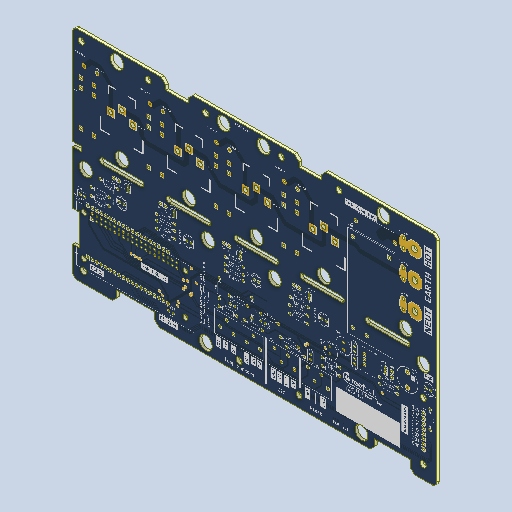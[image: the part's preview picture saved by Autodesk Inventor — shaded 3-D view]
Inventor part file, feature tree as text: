
AUTODESK INVENTOR PART (.ipt)
format: ipt  version: 2023.3 (Build 273359000, 359)  size: 3,891,712 bytes
history: native  units: in
note: dims shown in document units (in); Inventor stores cm internally (conversion verified against a paired STEP export)
features: sketch x301, hole x296, other x8, extrude x6
ambient origin geometry x8: Origin, YZ Plane, XZ Plane, XY Plane, X Axis, Y Axis, Z Axis, Center Point
bodies: Solid1 (feature_tree)
feature tree (611):
  other  "reefvolt_power_essentials_ESP32_BOARD"
  other  "BoardFrontPlane"
  extrude  "BoardOutline"  Depth=0.25in TaperAngle=0.0deg
  hole  "LED100-A"  [1 undecoded]
  hole  "LED100-K"  [1 undecoded]
  hole  "R409-2"  [1 undecoded]
  hole  "R409-1"  [1 undecoded]
  hole  "R408-2"  [1 undecoded]
  hole  "R408-1"  [1 undecoded]
  hole  "R401-2"  [1 undecoded]
  hole  "R401-1"  [1 undecoded]
  hole  "R400-2"  [1 undecoded]
  hole  "R400-1"  [1 undecoded]
  hole  "R407-1"  [1 undecoded]
  hole  "R407-2"  [1 undecoded]
  hole  "R406-1"  [1 undecoded]
  hole  "R406-2"  [1 undecoded]
  hole  "J403-4"  [1 undecoded]
  hole  "J403-3"  [1 undecoded]
  hole  "J403-2"  [1 undecoded]
  hole  "J403-1"  [1 undecoded]
  hole  "J400-4"  [1 undecoded]
  hole  "J400-3"  [1 undecoded]
  hole  "J400-2"  [1 undecoded]
  hole  "J400-1"  [1 undecoded]
  hole  "C400-1"  [1 undecoded]
  hole  "C400-2"  [1 undecoded]
  hole  "C402-1"  [1 undecoded]
  hole  "C402-2"  [1 undecoded]
  hole  "C401-1"  [1 undecoded]
  hole  "C401-2"  [1 undecoded]
  hole  "C301-1"  [1 undecoded]
  hole  "C301-2"  [1 undecoded]
  hole  "C300-1"  [1 undecoded]
  hole  "C300-2"  [1 undecoded]
  hole  "C103-1"  [1 undecoded]
  hole  "C103-2"  [1 undecoded]
  hole  "C102-1"  [1 undecoded]
  hole  "C102-2"  [1 undecoded]
  hole  "R405-2"  [1 undecoded]
  hole  "R405-1"  [1 undecoded]
  hole  "R404-2"  [1 undecoded]
  hole  "R404-1"  [1 undecoded]
  hole  "R403-1"  [1 undecoded]
  hole  "R403-2"  [1 undecoded]
  hole  "R402-1"  [1 undecoded]
  hole  "R402-2"  [1 undecoded]
  hole  "C101-1"  [1 undecoded]
  hole  "C101-2"  [1 undecoded]
  hole  "C100-2"  [1 undecoded]
  hole  "C100-1"  [1 undecoded]
  hole  "J402-3"  [1 undecoded]
  hole  "J402-2"  [1 undecoded]
  hole  "J402-1"  [1 undecoded]
  hole  "J401-3"  [1 undecoded]
  hole  "J401-2"  [1 undecoded]
  hole  "J401-1"  [1 undecoded]
  hole  "U301-J2-1"  [1 undecoded]
  hole  "U301-J2-2"  [1 undecoded]
  hole  "U301-J2-19"  [1 undecoded]
  hole  "U301-J2-3"  [1 undecoded]
  hole  "U301-J2-4"  [1 undecoded]
  hole  "U301-J2-5"  [1 undecoded]
  hole  "U301-J2-6"  [1 undecoded]
  hole  "U301-J2-7"  [1 undecoded]
  hole  "U301-J2-8"  [1 undecoded]
  hole  "U301-J2-9"  [1 undecoded]
  hole  "U301-J2-10"  [1 undecoded]
  hole  "U301-J2-11"  [1 undecoded]
  hole  "U301-J2-12"  [1 undecoded]
  hole  "U301-J2-13"  [1 undecoded]
  hole  "U301-J2-14"  [1 undecoded]
  hole  "U301-J2-15"  [1 undecoded]
  hole  "U301-J2-16"  [1 undecoded]
  hole  "U301-J2-17"  [1 undecoded]
  hole  "U301-J2-18"  [1 undecoded]
  hole  "U301-J3-1"  [1 undecoded]
  hole  "U301-J3-2"  [1 undecoded]
  hole  "U301-J3-3"  [1 undecoded]
  hole  "U301-J3-4"  [1 undecoded]
  hole  "U301-J3-5"  [1 undecoded]
  hole  "U301-J3-6"  [1 undecoded]
  hole  "U301-J3-7"  [1 undecoded]
  hole  "U301-J3-8"  [1 undecoded]
  hole  "U301-J3-9"  [1 undecoded]
  hole  "U301-J3-10"  [1 undecoded]
  hole  "U301-J3-11"  [1 undecoded]
  hole  "U301-J3-12"  [1 undecoded]
  hole  "U301-J3-13"  [1 undecoded]
  hole  "U301-J3-14"  [1 undecoded]
  hole  "U301-J3-15"  [1 undecoded]
  hole  "U301-J3-16"  [1 undecoded]
  hole  "U301-J3-17"  [1 undecoded]
  hole  "U301-J3-18"  [1 undecoded]
  hole  "U301-J3-19"  [1 undecoded]
  hole  "U300-4"  [1 undecoded]
  hole  "U300-3"  [1 undecoded]
  hole  "U300-2"  [1 undecoded]
  hole  "U300-1"  [1 undecoded]
  hole  "U300-_OMEBCNFT"  [1 undecoded]
  hole  "U300-_WJWYHENG"  [1 undecoded]
  hole  "U300-_VXPHIMLI"  [1 undecoded]
  hole  "U300-_OVXJNJRO"  [1 undecoded]
  hole  "U300-5"  [1 undecoded]
  hole  "U300-6"  [1 undecoded]
  hole  "U300-7"  [1 undecoded]
  hole  "U300-8"  [1 undecoded]
  hole  "U300-9"  [1 undecoded]
  hole  "U300-10"  [1 undecoded]
  hole  "U300-11"  [1 undecoded]
  hole  "U300-12"  [1 undecoded]
  hole  "U300-13"  [1 undecoded]
  hole  "U300-14"  [1 undecoded]
  hole  "U300-15"  [1 undecoded]
  hole  "U300-16"  [1 undecoded]
  hole  "U300-17"  [1 undecoded]
  hole  "U300-18"  [1 undecoded]
  hole  "U300-19"  [1 undecoded]
  hole  "U300-20"  [1 undecoded]
  hole  "U300-21"  [1 undecoded]
  hole  "U300-22"  [1 undecoded]
  hole  "U300-23"  [1 undecoded]
  hole  "U300-24"  [1 undecoded]
  hole  "U300-25"  [1 undecoded]
  hole  "U300-26"  [1 undecoded]
  hole  "U300-27"  [1 undecoded]
  hole  "U300-28"  [1 undecoded]
  hole  "U300-29"  [1 undecoded]
  hole  "U300-30"  [1 undecoded]
  hole  "U300-31"  [1 undecoded]
  hole  "U300-32"  [1 undecoded]
  hole  "U300-33"  [1 undecoded]
  hole  "U300-34"  [1 undecoded]
  hole  "U300-35"  [1 undecoded]
  hole  "U300-36"  [1 undecoded]
  hole  "U300-37"  [1 undecoded]
  hole  "U300-38"  [1 undecoded]
  hole  "U300-39"  [1 undecoded]
  hole  "U300-40"  [1 undecoded]
  hole  "Free-MNT+25_VMCLGUVO"  [1 undecoded]
  hole  "Free-MNT+26"  [1 undecoded]
  hole  "Free-MNT+25_KEWVVEYY"  [1 undecoded]
  hole  "Free-MNT+24"  [1 undecoded]
  hole  "Free-MNT+23"  [1 undecoded]
  hole  "Free-MNT+22"  [1 undecoded]
  hole  "Free-MNT+21"  [1 undecoded]
  hole  "Free-MNT+20"  [1 undecoded]
  hole  "Free-MNT+19"  [1 undecoded]
  hole  "Free-MNT+16"  [1 undecoded]
  hole  "J500-8"  [1 undecoded]
  hole  "J500-7"  [1 undecoded]
  hole  "J500-6"  [1 undecoded]
  hole  "J500-5"  [1 undecoded]
  hole  "J500-4"  [1 undecoded]
  hole  "J500-3"  [1 undecoded]
  hole  "J500-2"  [1 undecoded]
  hole  "J500-1"  [1 undecoded]
  hole  "U100-1"  [1 undecoded]
  hole  "U100-2"  [1 undecoded]
  hole  "U100-3"  [1 undecoded]
  hole  "Free-MNT+14_RVGMHBWC"  [1 undecoded]
  hole  "Free-MNT+14_EXUOOQPC"  [1 undecoded]
  hole  "Free-MNT+14_MIJJWCTW"  [1 undecoded]
  hole  "Free-MNT+14_XWPMBVWG"  [1 undecoded]
  hole  "Free-MNT+14_SCTWPPTG"  [1 undecoded]
  hole  "Free-MNT+14_UGSODQMV"  [1 undecoded]
  hole  "Free-MNT+7"  [1 undecoded]
  hole  "XF100-1"  [1 undecoded]
  hole  "XF100-2"  [1 undecoded]
  hole  "M200_PLD-1"  [1 undecoded]
  hole  "M200_PLD-2"  [1 undecoded]
  hole  "M200_PLC-2"  [1 undecoded]
  hole  "M200_PLC-1"  [1 undecoded]
  hole  "M200_PLB-1"  [1 undecoded]
  hole  "M200_PLB-2"  [1 undecoded]
  hole  "M200_PLA-2"  [1 undecoded]
  hole  "M200_PLA-1"  [1 undecoded]
  hole  "J200_PLD-3"  [1 undecoded]
  hole  "J200_PLD-2"  [1 undecoded]
  hole  "J200_PLD-1"  [1 undecoded]
  hole  "J200_PLC-1"  [1 undecoded]
  hole  "J200_PLC-2"  [1 undecoded]
  hole  "J200_PLC-3"  [1 undecoded]
  hole  "J200_PLB-3"  [1 undecoded]
  hole  "J200_PLB-2"  [1 undecoded]
  hole  "J200_PLB-1"  [1 undecoded]
  hole  "J200_PLA-1"  [1 undecoded]
  hole  "J200_PLA-2"  [1 undecoded]
  hole  "J200_PLA-3"  [1 undecoded]
  hole  "U101-4"  [1 undecoded]
  hole  "U101-3"  [1 undecoded]
  hole  "U101-2"  [1 undecoded]
  hole  "U101-1"  [1 undecoded]
  hole  "J_IN102-1"  [1 undecoded]
  hole  "J_IN102-2"  [1 undecoded]
  hole  "J_IN101-1"  [1 undecoded]
  hole  "J_IN101-2"  [1 undecoded]
  hole  "J_IN100-1"  [1 undecoded]
  hole  "J_IN100-2"  [1 undecoded]
  hole  "RL200_PLA-4"  [1 undecoded]
  hole  "RL200_PLA-5"  [1 undecoded]
  hole  "RL200_PLA-3"  [1 undecoded]
  hole  "RL200_PLA-6"  [1 undecoded]
  hole  "RL200_PLA-8"  [1 undecoded]
  hole  "RL200_PLA-1"  [1 undecoded]
  hole  "RL200_PLD-4"  [1 undecoded]
  hole  "RL200_PLD-5"  [1 undecoded]
  hole  "RL200_PLD-3"  [1 undecoded]
  hole  "RL200_PLD-6"  [1 undecoded]
  hole  "RL200_PLD-8"  [1 undecoded]
  hole  "RL200_PLD-1"  [1 undecoded]
  hole  "RL200_PLC-4"  [1 undecoded]
  hole  "RL200_PLC-5"  [1 undecoded]
  hole  "RL200_PLC-3"  [1 undecoded]
  hole  "RL200_PLC-6"  [1 undecoded]
  hole  "RL200_PLC-8"  [1 undecoded]
  hole  "RL200_PLC-1"  [1 undecoded]
  hole  "RL200_PLB-4"  [1 undecoded]
  hole  "RL200_PLB-5"  [1 undecoded]
  hole  "RL200_PLB-3"  [1 undecoded]
  hole  "RL200_PLB-6"  [1 undecoded]
  hole  "RL200_PLB-8"  [1 undecoded]
  hole  "RL200_PLB-1"  [1 undecoded]
  hole  "Free-MNT+14_KNTGPJBG"  [1 undecoded]
  hole  "Free-MNT+13"  [1 undecoded]
  hole  "Free-MNT+15"  [1 undecoded]
  hole  "Free-MNT+7_OGEKVTGU"  [1 undecoded]
  hole  "Free-MNT+7_ASLNLXPE"  [1 undecoded]
  hole  "SP400--"  [1 undecoded]
  hole  "SP400-+"  [1 undecoded]
  hole  "R411-2"  [1 undecoded]
  hole  "R411-1"  [1 undecoded]
  hole  "R410-2"  [1 undecoded]
  hole  "R410-1"  [1 undecoded]
  hole  "Q400-1"  [1 undecoded]
  hole  "Q400-2"  [1 undecoded]
  hole  "Q400-3"  [1 undecoded]
  hole  "D400-2"  [1 undecoded]
  hole  "D400-1"  [1 undecoded]
  hole  "R100-2"  [1 undecoded]
  hole  "R100-1"  [1 undecoded]
  extrude  "Free-MNT+11_RITJXHYI"  [1 undecoded]
  extrude  "Free-MNT+11_QMOWRTVF"  [1 undecoded]
  extrude  "Free-MNT+10"  [1 undecoded]
  extrude  "Free-MNT+9"  [1 undecoded]
  hole  "Free-MNT+14_SDQKQDHW"  [1 undecoded]
  hole  "Free-MNT+15_ENNIOCQM"  [1 undecoded]
  extrude  "Free-MNT+11_LVIULGXW"  [1 undecoded]
  hole  "Free-MNT+14_GXYHPMGR"  [1 undecoded]
  hole  "Free-MNT+14_QXCUKRLQ"  [1 undecoded]
  hole  "Free-MNT+14_BKPOHODQ"  [1 undecoded]
  hole  "Free-MNT+14_MHRQPGBW"  [1 undecoded]
  other  "Decal_Top"
  other  "Decal_Bottom"
  hole  "R202_PLD-2"  [1 undecoded]
  hole  "R202_PLD-1"  [1 undecoded]
  hole  "R202_PLC-2"  [1 undecoded]
  hole  "R202_PLC-1"  [1 undecoded]
  hole  "R202_PLB-2"  [1 undecoded]
  hole  "R202_PLB-1"  [1 undecoded]
  hole  "R202_PLA-2"  [1 undecoded]
  hole  "R202_PLA-1"  [1 undecoded]
  hole  "R201_PLD-1"  [1 undecoded]
  hole  "R201_PLD-2"  [1 undecoded]
  hole  "R201_PLC-2"  [1 undecoded]
  hole  "R201_PLC-1"  [1 undecoded]
  hole  "R201_PLB-1"  [1 undecoded]
  hole  "R201_PLB-2"  [1 undecoded]
  hole  "R201_PLA-2"  [1 undecoded]
  hole  "R201_PLA-1"  [1 undecoded]
  hole  "Q200_PLD-3"  [1 undecoded]
  hole  "Q200_PLD-2"  [1 undecoded]
  hole  "Q200_PLD-1"  [1 undecoded]
  hole  "Q200_PLC-1"  [1 undecoded]
  hole  "Q200_PLC-2"  [1 undecoded]
  hole  "Q200_PLC-3"  [1 undecoded]
  hole  "Q200_PLB-3"  [1 undecoded]
  hole  "Q200_PLB-2"  [1 undecoded]
  hole  "Q200_PLB-1"  [1 undecoded]
  hole  "Q200_PLA-1"  [1 undecoded]
  hole  "Q200_PLA-2"  [1 undecoded]
  hole  "Q200_PLA-3"  [1 undecoded]
  hole  "D200_PLD-1"  [1 undecoded]
  hole  "D200_PLD-2"  [1 undecoded]
  hole  "D200_PLC-2"  [1 undecoded]
  hole  "D200_PLC-1"  [1 undecoded]
  hole  "D200_PLB-1"  [1 undecoded]
  hole  "D200_PLB-2"  [1 undecoded]
  hole  "D200_PLA-1"  [1 undecoded]
  hole  "D200_PLA-2"  [1 undecoded]
  hole  "R200_PLD-1"  [1 undecoded]
  hole  "R200_PLD-2"  [1 undecoded]
  hole  "R200_PLC-2"  [1 undecoded]
  hole  "R200_PLC-1"  [1 undecoded]
  hole  "R200_PLB-1"  [1 undecoded]
  hole  "R200_PLB-2"  [1 undecoded]
  hole  "R200_PLA-2"  [1 undecoded]
  hole  "R200_PLA-1"  [1 undecoded]
  hole  "LED200_PLD-K"  [1 undecoded]
  hole  "LED200_PLD-A"  [1 undecoded]
  hole  "LED200_PLC-A"  [1 undecoded]
  hole  "LED200_PLC-K"  [1 undecoded]
  hole  "LED200_PLB-K"  [1 undecoded]
  hole  "LED200_PLB-A"  [1 undecoded]
  hole  "LED200_PLA-K"  [1 undecoded]
  hole  "LED200_PLA-A"  [1 undecoded]
  sketch  "Sketch61"  dims[d0=0.0614in d1=0.0in]
  sketch  "Sketch62"  dims[d405=0.032in d406=0.75in d407=0.375in d408=0.25in d409=0.5635in d410=1.0in d411=0.0in]
  sketch  "Sketch71"  dims[d412=0.032in d413=0.75in d414=0.375in d415=0.25in d416=0.5635in d417=1.0in d418=0.0in]
  sketch  "Sketch72"  dims[d475=0.032in d476=0.75in d477=0.375in d478=0.25in d479=0.5635in d480=1.0in d481=0.0in]
  sketch  "Sketch73"  dims[d482=0.032in d483=0.75in d484=0.375in d485=0.25in d486=0.5635in d487=1.0in d488=0.0in]
  sketch  "Sketch74"  dims[d489=0.032in d490=0.75in d491=0.375in d492=0.25in d493=0.5635in d494=1.0in d495=0.0in]
  sketch  "Sketch75"  dims[d496=0.032in d497=0.75in d498=0.375in d499=0.25in d500=0.5635in d501=1.0in d502=0.0in]
  sketch  "Sketch76"  dims[d503=0.032in d504=0.75in d505=0.375in d506=0.25in d507=0.5635in d508=1.0in d509=0.0in]
  sketch  "Sketch77"  dims[d510=0.032in d511=0.75in d512=0.375in d513=0.25in d514=0.5635in d515=1.0in d516=0.0in]
  sketch  "Sketch78"  dims[d517=0.032in d518=0.75in d519=0.375in d520=0.25in d521=0.5635in d522=1.0in d523=0.0in]
  sketch  "Sketch79"  dims[d524=0.032in d525=0.75in d526=0.375in d527=0.25in d528=0.5635in d529=1.0in d530=0.0in]
  sketch  "Sketch80"  dims[d531=0.032in d532=0.75in d533=0.375in d534=0.25in d535=0.5635in d536=1.0in d537=0.0in]
  sketch  "Sketch81"  dims[d538=0.032in d539=0.75in d540=0.375in d541=0.25in d542=0.5635in d543=1.0in d544=0.0in]
  sketch  "Sketch82"  dims[d545=0.032in d546=0.75in d547=0.375in d548=0.25in d549=0.5635in d550=1.0in d551=0.0in]
  sketch  "Sketch83"  dims[d552=0.032in d553=0.75in d554=0.375in d555=0.25in d556=0.5635in d557=1.0in d558=0.0in]
  sketch  "Sketch84"  dims[d559=0.0394in d560=0.75in d561=0.375in d562=0.25in d563=0.5635in d564=1.0in d565=0.0in]
  sketch  "Sketch85"  dims[d566=0.0394in d567=0.75in d568=0.375in d569=0.25in d570=0.5635in d571=1.0in d572=0.0in]
  sketch  "Sketch86"  dims[d573=0.0394in d574=0.75in d575=0.375in d576=0.25in d577=0.5635in d578=1.0in d579=0.0in]
  sketch  "Sketch87"  dims[d580=0.0394in d581=0.75in d582=0.375in d583=0.25in d584=0.5635in d585=1.0in d586=0.0in]
  sketch  "Sketch88"  dims[d587=0.0394in d588=0.75in d589=0.375in d590=0.25in d591=0.5635in d592=1.0in d593=0.0in]
  sketch  "Sketch89"  dims[d594=0.0394in d595=0.75in d596=0.375in d597=0.25in d598=0.5635in d599=1.0in d600=0.0in]
  sketch  "Sketch90"  dims[d601=0.0394in d602=0.75in d603=0.375in d604=0.25in d605=0.5635in d606=1.0in d607=0.0in]
  sketch  "Sketch91"  dims[d608=0.0394in d609=0.75in d610=0.375in d611=0.25in d612=0.5635in d613=1.0in d614=0.0in]
  sketch  "Sketch92"  dims[d615=0.0315in d616=0.75in d617=0.375in d618=0.25in d619=0.5635in d620=1.0in d621=0.0in]
  sketch  "Sketch93"  dims[d622=0.0315in d623=0.75in d624=0.375in d625=0.25in d626=0.5635in d627=1.0in d628=0.0in]
  sketch  "Sketch94"  dims[d629=0.0315in d630=0.75in d631=0.375in d632=0.25in d633=0.5635in d634=1.0in d635=0.0in]
  sketch  "Sketch95"  dims[d636=0.0315in d637=0.75in d638=0.375in d639=0.25in d640=0.5635in d641=1.0in d642=0.0in]
  sketch  "Sketch96"  dims[d643=0.0315in d644=0.75in d645=0.375in d646=0.25in d647=0.5635in d648=1.0in d649=0.0in]
  sketch  "Sketch97"  dims[d650=0.0315in d651=0.75in d652=0.375in d653=0.25in d654=0.5635in d655=1.0in d656=0.0in]
  sketch  "Sketch98"  dims[d657=0.0315in d658=0.75in d659=0.375in d660=0.25in d661=0.5635in d662=1.0in d663=0.0in]
  sketch  "Sketch99"  dims[d664=0.0315in d665=0.75in d666=0.375in d667=0.25in d668=0.5635in d669=1.0in d670=0.0in]
  sketch  "Sketch100"  dims[d671=0.0315in d672=0.75in d673=0.375in d674=0.25in d675=0.5635in d676=1.0in d677=0.0in]
  sketch  "Sketch101"  dims[d678=0.0315in d679=0.75in d680=0.375in d681=0.25in d682=0.5635in d683=1.0in d684=0.0in]
  sketch  "Sketch102"  dims[d685=0.0315in d686=0.75in d687=0.375in d688=0.25in d689=0.5635in d690=1.0in d691=0.0in]
  sketch  "Sketch103"  dims[d692=0.0315in d693=0.75in d694=0.375in d695=0.25in d696=0.5635in d697=1.0in d698=0.0in]
  sketch  "Sketch104"  dims[d699=0.0315in d700=0.75in d701=0.375in d702=0.25in d703=0.5635in d704=1.0in d705=0.0in]
  sketch  "Sketch105"  dims[d706=0.0315in d707=0.75in d708=0.375in d709=0.25in d710=0.5635in d711=1.0in d712=0.0in]
  sketch  "Sketch106"  dims[d713=0.032in d714=0.75in d715=0.375in d716=0.25in d717=0.5635in d718=1.0in d719=0.0in]
  sketch  "Sketch107"  dims[d720=0.032in d721=0.75in d722=0.375in d723=0.25in d724=0.5635in d725=1.0in d726=0.0in]
  sketch  "Sketch108"  dims[d727=0.032in d728=0.75in d729=0.375in d730=0.25in d731=0.5635in d732=1.0in d733=0.0in]
  sketch  "Sketch109"  dims[d734=0.032in d735=0.75in d736=0.375in d737=0.25in d738=0.5635in d739=1.0in d740=0.0in]
  sketch  "Sketch110"  dims[d741=0.032in d742=0.75in d743=0.375in d744=0.25in d745=0.5635in d746=1.0in d747=0.0in]
  sketch  "Sketch111"  dims[d748=0.032in d749=0.75in d750=0.375in d751=0.25in d752=0.5635in d753=1.0in d754=0.0in]
  sketch  "Sketch112"  dims[d755=0.032in d756=0.75in d757=0.375in d758=0.25in d759=0.5635in d760=1.0in d761=0.0in]
  sketch  "Sketch113"  dims[d762=0.032in d763=0.75in d764=0.375in d765=0.25in d766=0.5635in d767=1.0in d768=0.0in]
  sketch  "Sketch114"  dims[d769=0.0315in d770=0.75in d771=0.375in d772=0.25in d773=0.5635in d774=1.0in d775=0.0in]
  sketch  "Sketch115"  dims[d776=0.0315in d777=0.75in d778=0.375in d779=0.25in d780=0.5635in d781=1.0in d782=0.0in]
  sketch  "Sketch116"  dims[d783=0.0315in d784=0.75in d785=0.375in d786=0.25in d787=0.5635in d788=1.0in d789=0.0in]
  sketch  "Sketch117"  dims[d790=0.0315in d791=0.75in d792=0.375in d793=0.25in d794=0.5635in d795=1.0in d796=0.0in]
  sketch  "Sketch118"  dims[d797=0.0394in d798=0.75in d799=0.375in d800=0.25in d801=0.5635in d802=1.0in d803=0.0in]
  sketch  "Sketch119"  dims[d804=0.0394in d805=0.75in d806=0.375in d807=0.25in d808=0.5635in d809=1.0in d810=0.0in]
  sketch  "Sketch120"  dims[d811=0.0394in d812=0.75in d813=0.375in d814=0.25in d815=0.5635in d816=1.0in d817=0.0in]
  sketch  "Sketch121"  dims[d818=0.0394in d819=0.75in d820=0.375in d821=0.25in d822=0.5635in d823=1.0in d824=0.0in]
  sketch  "Sketch122"  dims[d825=0.0394in d826=0.75in d827=0.375in d828=0.25in d829=0.5635in d830=1.0in d831=0.0in]
  sketch  "Sketch123"  dims[d832=0.0394in d833=0.75in d834=0.375in d835=0.25in d836=0.5635in d837=1.0in d838=0.0in]
  sketch  "Sketch124"  dims[d839=0.0409in d840=0.75in d841=0.375in d842=0.25in d843=0.5635in d844=1.0in d845=0.0in]
  sketch  "Sketch125"  dims[d846=0.0409in d847=0.75in d848=0.375in d849=0.25in d850=0.5635in d851=1.0in d852=0.0in]
  sketch  "Sketch126"  dims[d853=0.0409in d854=0.75in d855=0.375in d856=0.25in d857=0.5635in d858=1.0in d859=0.0in]
  sketch  "Sketch127"  dims[d860=0.0409in d861=0.75in d862=0.375in d863=0.25in d864=0.5635in d865=1.0in d866=0.0in]
  sketch  "Sketch128"  dims[d867=0.0409in d868=0.75in d869=0.375in d870=0.25in d871=0.5635in d872=1.0in d873=0.0in]
  sketch  "Sketch129"  dims[d874=0.0409in d875=0.75in d876=0.375in d877=0.25in d878=0.5635in d879=1.0in d880=0.0in]
  sketch  "Sketch130"  dims[d881=0.0409in d882=0.75in d883=0.375in d884=0.25in d885=0.5635in d886=1.0in d887=0.0in]
  sketch  "Sketch131"  dims[d888=0.0409in d889=0.75in d890=0.375in d891=0.25in d892=0.5635in d893=1.0in d894=0.0in]
  sketch  "Sketch132"  dims[d895=0.0409in d896=0.75in d897=0.375in d898=0.25in d899=0.5635in d900=1.0in d901=0.0in]
  sketch  "Sketch133"  dims[d902=0.0409in d903=0.75in d904=0.375in d905=0.25in d906=0.5635in d907=1.0in d908=0.0in]
  sketch  "Sketch134"  dims[d909=0.0409in d910=0.75in d911=0.375in d912=0.25in d913=0.5635in d914=1.0in d915=0.0in]
  sketch  "Sketch135"  dims[d916=0.0409in d917=0.75in d918=0.375in d919=0.25in d920=0.5635in d921=1.0in d922=0.0in]
  sketch  "Sketch136"  dims[d923=0.0409in d924=0.75in d925=0.375in d926=0.25in d927=0.5635in d928=1.0in d929=0.0in]
  sketch  "Sketch137"  dims[d930=0.0409in d931=0.75in d932=0.375in d933=0.25in d934=0.5635in d935=1.0in d936=0.0in]
  sketch  "Sketch138"  dims[d937=0.0409in d938=0.75in d939=0.375in d940=0.25in d941=0.5635in d942=1.0in d943=0.0in]
  sketch  "Sketch139"  dims[d944=0.0409in d945=0.75in d946=0.375in d947=0.25in d948=0.5635in d949=1.0in d950=0.0in]
  sketch  "Sketch140"  dims[d951=0.0409in d952=0.75in d953=0.375in d954=0.25in d955=0.5635in d956=1.0in d957=0.0in]
  sketch  "Sketch141"  dims[d958=0.0409in d959=0.75in d960=0.375in d961=0.25in d962=0.5635in d963=1.0in d964=0.0in]
  sketch  "Sketch142"  dims[d965=0.0409in d966=0.75in d967=0.375in d968=0.25in d969=0.5635in d970=1.0in d971=0.0in]
  sketch  "Sketch143"  dims[d972=0.0409in d973=0.75in d974=0.375in d975=0.25in d976=0.5635in d977=1.0in d978=0.0in]
  sketch  "Sketch144"  dims[d979=0.0409in d980=0.75in d981=0.375in d982=0.25in d983=0.5635in d984=1.0in d985=0.0in]
  sketch  "Sketch145"  dims[d986=0.0409in d987=0.75in d988=0.375in d989=0.25in d990=0.5635in d991=1.0in d992=0.0in]
  sketch  "Sketch146"  dims[d993=0.0409in d994=0.75in d995=0.375in d996=0.25in d997=0.5635in d998=1.0in d999=0.0in]
  sketch  "Sketch147"  dims[d1000=0.0409in d1001=0.75in d1002=0.375in d1003=0.25in d1004=0.5635in d1005=1.0in d1006=0.0in]
  sketch  "Sketch148"  dims[d1007=0.0409in d1008=0.75in d1009=0.375in d1010=0.25in d1011=0.5635in d1012=1.0in d1013=0.0in]
  sketch  "Sketch149"  dims[d1014=0.0409in d1015=0.75in d1016=0.375in d1017=0.25in d1018=0.5635in d1019=1.0in d1020=0.0in]
  sketch  "Sketch150"  dims[d1021=0.0409in d1022=0.75in d1023=0.375in d1024=0.25in d1025=0.5635in d1026=1.0in d1027=0.0in]
  sketch  "Sketch151"  dims[d1028=0.0409in d1029=0.75in d1030=0.375in d1031=0.25in d1032=0.5635in d1033=1.0in d1034=0.0in]
  sketch  "Sketch152"  dims[d1035=0.0409in d1036=0.75in d1037=0.375in d1038=0.25in d1039=0.5635in d1040=1.0in d1041=0.0in]
  sketch  "Sketch153"  dims[d1042=0.0409in d1043=0.75in d1044=0.375in d1045=0.25in d1046=0.5635in d1047=1.0in d1048=0.0in]
  sketch  "Sketch154"  dims[d1049=0.0409in d1050=0.75in d1051=0.375in d1052=0.25in d1053=0.5635in d1054=1.0in d1055=0.0in]
  sketch  "Sketch155"  dims[d1056=0.0409in d1057=0.75in d1058=0.375in d1059=0.25in d1060=0.5635in d1061=1.0in d1062=0.0in]
  sketch  "Sketch156"  dims[d1063=0.0409in d1064=0.75in d1065=0.375in d1066=0.25in d1067=0.5635in d1068=1.0in d1069=0.0in]
  sketch  "Sketch157"  dims[d1070=0.0409in d1071=0.75in d1072=0.375in d1073=0.25in d1074=0.5635in d1075=1.0in d1076=0.0in]
  sketch  "Sketch158"  dims[d1077=0.0409in d1078=0.75in d1079=0.375in d1080=0.25in d1081=0.5635in d1082=1.0in d1083=0.0in]
  sketch  "Sketch159"  dims[d1084=0.0409in d1085=0.75in d1086=0.375in d1087=0.25in d1088=0.5635in d1089=1.0in d1090=0.0in]
  sketch  "Sketch160"  dims[d1091=0.0409in d1092=0.75in d1093=0.375in d1094=0.25in d1095=0.5635in d1096=1.0in d1097=0.0in]
  sketch  "Sketch161"  dims[d1098=0.0409in d1099=0.75in d1100=0.375in d1101=0.25in d1102=0.5635in d1103=1.0in d1104=0.0in]
  sketch  "Sketch162"  dims[d1105=0.04in d1106=0.75in d1107=0.375in d1108=0.25in d1109=0.5635in d1110=1.0in d1111=0.0in]
  sketch  "Sketch163"  dims[d1112=0.04in d1113=0.75in d1114=0.375in d1115=0.25in d1116=0.5635in d1117=1.0in d1118=0.0in]
  sketch  "Sketch164"  dims[d1119=0.04in d1120=0.75in d1121=0.375in d1122=0.25in d1123=0.5635in d1124=1.0in d1125=0.0in]
  sketch  "Sketch165"  dims[d1126=0.04in d1127=0.75in d1128=0.375in d1129=0.25in d1130=0.5635in d1131=1.0in d1132=0.0in]
  sketch  "Sketch166"  dims[d1133=0.1083in d1134=0.75in d1135=0.375in d1136=0.25in d1137=0.5635in d1138=1.0in d1139=0.0in]
  sketch  "Sketch167"  dims[d1140=0.1083in d1141=0.75in d1142=0.375in d1143=0.25in d1144=0.5635in d1145=1.0in d1146=0.0in]
  sketch  "Sketch168"  dims[d1147=0.1083in d1148=0.75in d1149=0.375in d1150=0.25in d1151=0.5635in d1152=1.0in d1153=0.0in]
  sketch  "Sketch169"  dims[d1154=0.1083in d1155=0.75in d1156=0.375in d1157=0.25in d1158=0.5635in d1159=1.0in d1160=0.0in]
  sketch  "Sketch170"  dims[d1161=0.04in d1162=0.75in d1163=0.375in d1164=0.25in d1165=0.5635in d1166=1.0in d1167=0.0in]
  sketch  "Sketch171"  dims[d1168=0.04in d1169=0.75in d1170=0.375in d1171=0.25in d1172=0.5635in d1173=1.0in d1174=0.0in]
  sketch  "Sketch172"  dims[d1175=0.04in d1176=0.75in d1177=0.375in d1178=0.25in d1179=0.5635in d1180=1.0in d1181=0.0in]
  sketch  "Sketch173"  dims[d1182=0.04in d1183=0.75in d1184=0.375in d1185=0.25in d1186=0.5635in d1187=1.0in d1188=0.0in]
  sketch  "Sketch174"  dims[d1189=0.04in d1190=0.75in d1191=0.375in d1192=0.25in d1193=0.5635in d1194=1.0in d1195=0.0in]
  sketch  "Sketch175"  dims[d1196=0.04in d1197=0.75in d1198=0.375in d1199=0.25in d1200=0.5635in d1201=1.0in d1202=0.0in]
  sketch  "Sketch176"  dims[d1203=0.04in d1204=0.75in d1205=0.375in d1206=0.25in d1207=0.5635in d1208=1.0in d1209=0.0in]
  sketch  "Sketch177"  dims[d1210=0.04in d1211=0.75in d1212=0.375in d1213=0.25in d1214=0.5635in d1215=1.0in d1216=0.0in]
  sketch  "Sketch178"  dims[d1217=0.04in d1218=0.75in d1219=0.375in d1220=0.25in d1221=0.5635in d1222=1.0in d1223=0.0in]
  sketch  "Sketch179"  dims[d1224=0.04in d1225=0.75in d1226=0.375in d1227=0.25in d1228=0.5635in d1229=1.0in d1230=0.0in]
  sketch  "Sketch180"  dims[d1231=0.04in d1232=0.75in d1233=0.375in d1234=0.25in d1235=0.5635in d1236=1.0in d1237=0.0in]
  sketch  "Sketch181"  dims[d1238=0.04in d1239=0.75in d1240=0.375in d1241=0.25in d1242=0.5635in d1243=1.0in d1244=0.0in]
  sketch  "Sketch182"  dims[d1245=0.04in d1246=0.75in d1247=0.375in d1248=0.25in d1249=0.5635in d1250=1.0in d1251=0.0in]
  sketch  "Sketch183"  dims[d1252=0.04in d1253=0.75in d1254=0.375in d1255=0.25in d1256=0.5635in d1257=1.0in d1258=0.0in]
  sketch  "Sketch184"  dims[d1259=0.04in d1260=0.75in d1261=0.375in d1262=0.25in d1263=0.5635in d1264=1.0in d1265=0.0in]
  sketch  "Sketch185"  dims[d1266=0.04in d1267=0.75in d1268=0.375in d1269=0.25in d1270=0.5635in d1271=1.0in d1272=0.0in]
  sketch  "Sketch186"  dims[d1273=0.04in d1274=0.75in d1275=0.375in d1276=0.25in d1277=0.5635in d1278=1.0in d1279=0.0in]
  sketch  "Sketch187"  dims[d1280=0.04in d1281=0.75in d1282=0.375in d1283=0.25in d1284=0.5635in d1285=1.0in d1286=0.0in]
  sketch  "Sketch188"  dims[d1287=0.04in d1288=0.75in d1289=0.375in d1290=0.25in d1291=0.5635in d1292=1.0in d1293=0.0in]
  sketch  "Sketch189"  dims[d1294=0.04in d1295=0.75in d1296=0.375in d1297=0.25in d1298=0.5635in d1299=1.0in d1300=0.0in]
  sketch  "Sketch190"  dims[d1301=0.04in d1302=0.75in d1303=0.375in d1304=0.25in d1305=0.5635in d1306=1.0in d1307=0.0in]
  sketch  "Sketch191"  dims[d1308=0.04in d1309=0.75in d1310=0.375in d1311=0.25in d1312=0.5635in d1313=1.0in d1314=0.0in]
  sketch  "Sketch192"  dims[d1315=0.04in d1316=0.75in d1317=0.375in d1318=0.25in d1319=0.5635in d1320=1.0in d1321=0.0in]
  sketch  "Sketch193"  dims[d1322=0.04in d1323=0.75in d1324=0.375in d1325=0.25in d1326=0.5635in d1327=1.0in d1328=0.0in]
  sketch  "Sketch194"  dims[d1329=0.04in d1330=0.75in d1331=0.375in d1332=0.25in d1333=0.5635in d1334=1.0in d1335=0.0in]
  sketch  "Sketch195"  dims[d1336=0.04in d1337=0.75in d1338=0.375in d1339=0.25in d1340=0.5635in d1341=1.0in d1342=0.0in]
  sketch  "Sketch196"  dims[d1343=0.04in d1344=0.75in d1345=0.375in d1346=0.25in d1347=0.5635in d1348=1.0in d1349=0.0in]
  sketch  "Sketch197"  dims[d1350=0.04in d1351=0.75in d1352=0.375in d1353=0.25in d1354=0.5635in d1355=1.0in d1356=0.0in]
  sketch  "Sketch198"  dims[d1357=0.04in d1358=0.75in d1359=0.375in d1360=0.25in d1361=0.5635in d1362=1.0in d1363=0.0in]
  sketch  "Sketch199"  dims[d1364=0.04in d1365=0.75in d1366=0.375in d1367=0.25in d1368=0.5635in d1369=1.0in d1370=0.0in]
  sketch  "Sketch200"  dims[d1371=0.04in d1372=0.75in d1373=0.375in d1374=0.25in d1375=0.5635in d1376=1.0in d1377=0.0in]
  sketch  "Sketch201"  dims[d1378=0.04in d1379=0.75in d1380=0.375in d1381=0.25in d1382=0.5635in d1383=1.0in d1384=0.0in]
  sketch  "Sketch202"  dims[d1385=0.04in d1386=0.75in d1387=0.375in d1388=0.25in d1389=0.5635in d1390=1.0in d1391=0.0in]
  sketch  "Sketch203"  dims[d1392=0.04in d1393=0.75in d1394=0.375in d1395=0.25in d1396=0.5635in d1397=1.0in d1398=0.0in]
  sketch  "Sketch204"  dims[d1399=0.04in d1400=0.75in d1401=0.375in d1402=0.25in d1403=0.5635in d1404=1.0in d1405=0.0in]
  sketch  "Sketch253"  dims[d1406=0.04in d1407=0.75in d1408=0.375in d1409=0.25in d1410=0.5635in d1411=1.0in d1412=0.0in]
  sketch  "Sketch261"  dims[d1749=0.1339in d1750=0.75in d1751=0.375in d1752=0.25in d1753=0.5635in d1754=1.0in d1755=0.0in]
  sketch  "Sketch262"  dims[d1805=0.1339in d1806=0.75in d1807=0.375in d1808=0.25in d1809=0.5635in d1810=1.0in d1811=0.0in]
  sketch  "Sketch263"  dims[d1812=0.1339in d1813=0.75in d1814=0.375in d1815=0.25in d1816=0.5635in d1817=1.0in d1818=0.0in]
  sketch  "Sketch264"  dims[d1819=0.1339in d1820=0.75in d1821=0.375in d1822=0.25in d1823=0.5635in d1824=1.0in d1825=0.0in]
  sketch  "Sketch265"  dims[d1826=0.1339in d1827=0.75in d1828=0.375in d1829=0.25in d1830=0.5635in d1831=1.0in d1832=0.0in]
  sketch  "Sketch266"  dims[d1833=0.1339in d1834=0.75in d1835=0.375in d1836=0.25in d1837=0.5635in d1838=1.0in d1839=0.0in]
  sketch  "Sketch267"  dims[d1840=0.1339in d1841=0.75in d1842=0.375in d1843=0.25in d1844=0.5635in d1845=1.0in d1846=0.0in]
  sketch  "Sketch268"  dims[d1847=0.1339in d1848=0.75in d1849=0.375in d1850=0.25in d1851=0.5635in d1852=1.0in d1853=0.0in]
  sketch  "Sketch270"  dims[d1854=0.1339in d1855=0.75in d1856=0.375in d1857=0.25in d1858=0.5635in d1859=1.0in d1860=0.0in]
  sketch  "Sketch284"  dims[d1868=0.1339in d1869=0.75in d1870=0.375in d1871=0.25in d1872=0.5635in d1873=1.0in d1874=0.0in]
  sketch  "Sketch285"  dims[d1941=0.04in d1942=0.75in d1943=0.375in d1944=0.25in d1945=0.5635in d1946=1.0in d1947=0.0in]
  sketch  "Sketch286"  dims[d1948=0.04in d1949=0.75in d1950=0.375in d1951=0.25in d1952=0.5635in d1953=1.0in d1954=0.0in]
  sketch  "Sketch287"  dims[d1955=0.04in d1956=0.75in d1957=0.375in d1958=0.25in d1959=0.5635in d1960=1.0in d1961=0.0in]
  sketch  "Sketch288"  dims[d1962=0.04in d1963=0.75in d1964=0.375in d1965=0.25in d1966=0.5635in d1967=1.0in d1968=0.0in]
  sketch  "Sketch289"  dims[d1969=0.04in d1970=0.75in d1971=0.375in d1972=0.25in d1973=0.5635in d1974=1.0in d1975=0.0in]
  sketch  "Sketch290"  dims[d1976=0.04in d1977=0.75in d1978=0.375in d1979=0.25in d1980=0.5635in d1981=1.0in d1982=0.0in]
  sketch  "Sketch291"  dims[d1983=0.04in d1984=0.75in d1985=0.375in d1986=0.25in d1987=0.5635in d1988=1.0in d1989=0.0in]
  sketch  "Sketch294"  dims[d1990=0.04in d1991=0.75in d1992=0.375in d1993=0.25in d1994=0.5635in d1995=1.0in d1996=0.0in]
  sketch  "Sketch295"  dims[d2001=0.0394in d2002=0.75in d2003=0.375in d2004=0.25in d2005=0.5635in d2006=1.0in d2007=0.0in]
  sketch  "Sketch296"  dims[d2008=0.0394in d2009=0.75in d2010=0.375in d2011=0.25in d2012=0.5635in d2013=1.0in d2014=0.0in]
  sketch  "Sketch315"  dims[d2015=0.0394in d2016=0.75in d2017=0.375in d2018=0.25in d2019=0.5635in d2020=1.0in d2021=0.0in]
  sketch  "Sketch316"  dims[d2128=0.2953in d2129=0.75in d2130=0.375in d2131=0.25in d2132=0.5635in d2133=1.0in d2134=0.0in]
  sketch  "Sketch317"  dims[d2135=0.2953in d2136=0.75in d2137=0.375in d2138=0.25in d2139=0.5635in d2140=1.0in d2141=0.0in]
  sketch  "Sketch318"  dims[d2142=0.2953in d2143=0.75in d2144=0.375in d2145=0.25in d2146=0.5635in d2147=1.0in d2148=0.0in]
  sketch  "Sketch319"  dims[d2149=0.2953in d2150=0.75in d2151=0.375in d2152=0.25in d2153=0.5635in d2154=1.0in d2155=0.0in]
  sketch  "Sketch320"  dims[d2156=0.2953in d2157=0.75in d2158=0.375in d2159=0.25in d2160=0.5635in d2161=1.0in d2162=0.0in]
  sketch  "Sketch359"  dims[d2163=0.2953in d2164=0.75in d2165=0.375in d2166=0.25in d2167=0.5635in d2168=1.0in d2169=0.0in]
  sketch  "Sketch373"  dims[d2406=0.1378in d2407=0.75in d2408=0.375in d2409=0.25in d2410=0.5635in d2411=1.0in d2412=0.0in]
  sketch  "Sketch374"  dims[d2476=0.0512in d2477=0.75in d2478=0.375in d2479=0.25in d2480=0.5635in d2481=1.0in d2482=0.0in]
  sketch  "Sketch375"  dims[d2483=0.0512in d2484=0.75in d2485=0.375in d2486=0.25in d2487=0.5635in d2488=1.0in d2489=0.0in]
  sketch  "Sketch376"  dims[d2490=0.0354in d2491=0.75in d2492=0.375in d2493=0.25in d2494=0.5635in d2495=1.0in d2496=0.0in]
  sketch  "Sketch377"  dims[d2497=0.0354in d2498=0.75in d2499=0.375in d2500=0.25in d2501=0.5635in d2502=1.0in d2503=0.0in]
  sketch  "Sketch378"  dims[d2504=0.0354in d2505=0.75in d2506=0.375in d2507=0.25in d2508=0.5635in d2509=1.0in d2510=0.0in]
  sketch  "Sketch379"  dims[d2511=0.0354in d2512=0.75in d2513=0.375in d2514=0.25in d2515=0.5635in d2516=1.0in d2517=0.0in]
  sketch  "Sketch380"  dims[d2518=0.0354in d2519=0.75in d2520=0.375in d2521=0.25in d2522=0.5635in d2523=1.0in d2524=0.0in]
  sketch  "Sketch381"  dims[d2525=0.0354in d2526=0.75in d2527=0.375in d2528=0.25in d2529=0.5635in d2530=1.0in d2531=0.0in]
  sketch  "Sketch382"  dims[d2532=0.0354in d2533=0.75in d2534=0.375in d2535=0.25in d2536=0.5635in d2537=1.0in d2538=0.0in]
  sketch  "Sketch383"  dims[d2539=0.0354in d2540=0.75in d2541=0.375in d2542=0.25in d2543=0.5635in d2544=1.0in d2545=0.0in]
  sketch  "Sketch384"  dims[d2546=0.0984in d2547=0.75in d2548=0.375in d2549=0.25in d2550=0.5635in d2551=1.0in d2552=0.0in]
  sketch  "Sketch385"  dims[d2553=0.0984in d2554=0.75in d2555=0.375in d2556=0.25in d2557=0.5635in d2558=1.0in d2559=0.0in]
  sketch  "Sketch386"  dims[d2560=0.0984in d2561=0.75in d2562=0.375in d2563=0.25in d2564=0.5635in d2565=1.0in d2566=0.0in]
  sketch  "Sketch387"  dims[d2567=0.0984in d2568=0.75in d2569=0.375in d2570=0.25in d2571=0.5635in d2572=1.0in d2573=0.0in]
  sketch  "Sketch388"  dims[d2574=0.0984in d2575=0.75in d2576=0.375in d2577=0.25in d2578=0.5635in d2579=1.0in d2580=0.0in]
  sketch  "Sketch389"  dims[d2581=0.0984in d2582=0.75in d2583=0.375in d2584=0.25in d2585=0.5635in d2586=1.0in d2587=0.0in]
  sketch  "Sketch390"  dims[d2588=0.0984in d2589=0.75in d2590=0.375in d2591=0.25in d2592=0.5635in d2593=1.0in d2594=0.0in]
  sketch  "Sketch391"  dims[d2595=0.0984in d2596=0.75in d2597=0.375in d2598=0.25in d2599=0.5635in d2600=1.0in d2601=0.0in]
  sketch  "Sketch392"  dims[d2602=0.0984in d2603=0.75in d2604=0.375in d2605=0.25in d2606=0.5635in d2607=1.0in d2608=0.0in]
  sketch  "Sketch393"  dims[d2609=0.0984in d2610=0.75in d2611=0.375in d2612=0.25in d2613=0.5635in d2614=1.0in d2615=0.0in]
  sketch  "Sketch394"  dims[d2616=0.0984in d2617=0.75in d2618=0.375in d2619=0.25in d2620=0.5635in d2621=1.0in d2622=0.0in]
  sketch  "Sketch395"  dims[d2623=0.0984in d2624=0.75in d2625=0.375in d2626=0.25in d2627=0.5635in d2628=1.0in d2629=0.0in]
  sketch  "Sketch396"  dims[d2630=0.0512in d2631=0.75in d2632=0.375in d2633=0.25in d2634=0.5635in d2635=1.0in d2636=0.0in]
  sketch  "Sketch397"  dims[d2637=0.0512in d2638=0.75in d2639=0.375in d2640=0.25in d2641=0.5635in d2642=1.0in d2643=0.0in]
  sketch  "Sketch398"  dims[d2644=0.0512in d2645=0.75in d2646=0.375in d2647=0.25in d2648=0.5635in d2649=1.0in d2650=0.0in]
  sketch  "Sketch399"  dims[d2651=0.0512in d2652=0.75in d2653=0.375in d2654=0.25in d2655=0.5635in d2656=1.0in d2657=0.0in]
  sketch  "Sketch400"  dims[d2658=0.0591in d2659=0.75in d2660=0.375in d2661=0.25in d2662=0.5635in d2663=1.0in d2664=0.0in]
  sketch  "Sketch401"  dims[d2665=0.0591in d2666=0.75in d2667=0.375in d2668=0.25in d2669=0.5635in d2670=1.0in d2671=0.0in]
  sketch  "Sketch402"  dims[d2672=0.0591in d2673=0.75in d2674=0.375in d2675=0.25in d2676=0.5635in d2677=1.0in d2678=0.0in]
  sketch  "Sketch403"  dims[d2679=0.0591in d2680=0.75in d2681=0.375in d2682=0.25in d2683=0.5635in d2684=1.0in d2685=0.0in]
  sketch  "Sketch404"  dims[d2686=0.0591in d2687=0.75in d2688=0.375in d2689=0.25in d2690=0.5635in d2691=1.0in d2692=0.0in]
  sketch  "Sketch405"  dims[d2693=0.0591in d2694=0.75in d2695=0.375in d2696=0.25in d2697=0.5635in d2698=1.0in d2699=0.0in]
  sketch  "Sketch406"  dims[d2700=0.0512in d2701=0.75in d2702=0.375in d2703=0.25in d2704=0.5635in d2705=1.0in d2706=0.0in]
  sketch  "Sketch407"  dims[d2707=0.0512in d2708=0.75in d2709=0.375in d2710=0.25in d2711=0.5635in d2712=1.0in d2713=0.0in]
  sketch  "Sketch408"  dims[d2714=0.0512in d2715=0.75in d2716=0.375in d2717=0.25in d2718=0.5635in d2719=1.0in d2720=0.0in]
  sketch  "Sketch409"  dims[d2721=0.0512in d2722=0.75in d2723=0.375in d2724=0.25in d2725=0.5635in d2726=1.0in d2727=0.0in]
  sketch  "Sketch410"  dims[d2728=0.0512in d2729=0.75in d2730=0.375in d2731=0.25in d2732=0.5635in d2733=1.0in d2734=0.0in]
  sketch  "Sketch411"  dims[d2735=0.0512in d2736=0.75in d2737=0.375in d2738=0.25in d2739=0.5635in d2740=1.0in d2741=0.0in]
  sketch  "Sketch412"  dims[d2742=0.0512in d2743=0.75in d2744=0.375in d2745=0.25in d2746=0.5635in d2747=1.0in d2748=0.0in]
  sketch  "Sketch413"  dims[d2749=0.0512in d2750=0.75in d2751=0.375in d2752=0.25in d2753=0.5635in d2754=1.0in d2755=0.0in]
  sketch  "Sketch414"  dims[d2756=0.0512in d2757=0.75in d2758=0.375in d2759=0.25in d2760=0.5635in d2761=1.0in d2762=0.0in]
  sketch  "Sketch415"  dims[d2763=0.0512in d2764=0.75in d2765=0.375in d2766=0.25in d2767=0.5635in d2768=1.0in d2769=0.0in]
  sketch  "Sketch416"  dims[d2770=0.0512in d2771=0.75in d2772=0.375in d2773=0.25in d2774=0.5635in d2775=1.0in d2776=0.0in]
  sketch  "Sketch417"  dims[d2777=0.0512in d2778=0.75in d2779=0.375in d2780=0.25in d2781=0.5635in d2782=1.0in d2783=0.0in]
  sketch  "Sketch418"  dims[d2784=0.0512in d2785=0.75in d2786=0.375in d2787=0.25in d2788=0.5635in d2789=1.0in d2790=0.0in]
  sketch  "Sketch419"  dims[d2791=0.0512in d2792=0.75in d2793=0.375in d2794=0.25in d2795=0.5635in d2796=1.0in d2797=0.0in]
  sketch  "Sketch420"  dims[d2798=0.0512in d2799=0.75in d2800=0.375in d2801=0.25in d2802=0.5635in d2803=1.0in d2804=0.0in]
  sketch  "Sketch421"  dims[d2805=0.0512in d2806=0.75in d2807=0.375in d2808=0.25in d2809=0.5635in d2810=1.0in d2811=0.0in]
  sketch  "Sketch422"  dims[d2812=0.0512in d2813=0.75in d2814=0.375in d2815=0.25in d2816=0.5635in d2817=1.0in d2818=0.0in]
  sketch  "Sketch423"  dims[d2819=0.0512in d2820=0.75in d2821=0.375in d2822=0.25in d2823=0.5635in d2824=1.0in d2825=0.0in]
  sketch  "Sketch424"  dims[d2826=0.0512in d2827=0.75in d2828=0.375in d2829=0.25in d2830=0.5635in d2831=1.0in d2832=0.0in]
  sketch  "Sketch425"  dims[d2833=0.0512in d2834=0.75in d2835=0.375in d2836=0.25in d2837=0.5635in d2838=1.0in d2839=0.0in]
  sketch  "Sketch426"  dims[d2840=0.0512in d2841=0.75in d2842=0.375in d2843=0.25in d2844=0.5635in d2845=1.0in d2846=0.0in]
  sketch  "Sketch427"  dims[d2847=0.0512in d2848=0.75in d2849=0.375in d2850=0.25in d2851=0.5635in d2852=1.0in d2853=0.0in]
  sketch  "Sketch428"  dims[d2854=0.0512in d2855=0.75in d2856=0.375in d2857=0.25in d2858=0.5635in d2859=1.0in d2860=0.0in]
  sketch  "Sketch429"  dims[d2861=0.0512in d2862=0.75in d2863=0.375in d2864=0.25in d2865=0.5635in d2866=1.0in d2867=0.0in]
  sketch  "Sketch430"  dims[d2868=0.2953in d2869=0.75in d2870=0.375in d2871=0.25in d2872=0.5635in d2873=1.0in d2874=0.0in]
  sketch  "Sketch431"  dims[d2875=0.2953in d2876=0.75in d2877=0.375in d2878=0.25in d2879=0.5635in d2880=1.0in d2881=0.0in]
  sketch  "Sketch432"  dims[d2882=0.2953in d2883=0.75in d2884=0.375in d2885=0.25in d2886=0.5635in d2887=1.0in d2888=0.0in]
  sketch  "Sketch433"  dims[d2889=0.1378in d2890=0.75in d2891=0.375in d2892=0.25in d2893=0.5635in d2894=1.0in d2895=0.0in]
  sketch  "Sketch436"  dims[d2896=0.1378in d2897=0.75in d2898=0.375in d2899=0.25in d2900=0.5635in d2901=1.0in d2902=0.0in]
  sketch  "Sketch437"  dims[d2907=0.0315in d2908=0.75in d2909=0.375in d2910=0.25in d2911=0.5635in d2912=1.0in d2913=0.0in]
  sketch  "Sketch438"  dims[d2914=0.0315in d2915=0.75in d2916=0.375in d2917=0.25in d2918=0.5635in d2919=1.0in d2920=0.0in]
  sketch  "Sketch439"  dims[d2921=0.032in d2922=0.75in d2923=0.375in d2924=0.25in d2925=0.5635in d2926=1.0in d2927=0.0in]
  sketch  "Sketch440"  dims[d2928=0.032in d2929=0.75in d2930=0.375in d2931=0.25in d2932=0.5635in d2933=1.0in d2934=0.0in]
  sketch  "Sketch441"  dims[d2935=0.032in d2936=0.75in d2937=0.375in d2938=0.25in d2939=0.5635in d2940=1.0in d2941=0.0in]
  sketch  "Sketch442"  dims[d2942=0.032in d2943=0.75in d2944=0.375in d2945=0.25in d2946=0.5635in d2947=1.0in d2948=0.0in]
  sketch  "Sketch443"  dims[d2949=0.0315in d2950=0.75in d2951=0.375in d2952=0.25in d2953=0.5635in d2954=1.0in d2955=0.0in]
  sketch  "Sketch444"  dims[d2956=0.0315in d2957=0.75in d2958=0.375in d2959=0.25in d2960=0.5635in d2961=1.0in d2962=0.0in]
  sketch  "Sketch445"  dims[d2963=0.0315in d2964=0.75in d2965=0.375in d2966=0.25in d2967=0.5635in d2968=1.0in d2969=0.0in]
  sketch  "Sketch446"  dims[d2970=0.0453in d2971=0.75in d2972=0.375in d2973=0.25in d2974=0.5635in d2975=1.0in d2976=0.0in]
  sketch  "Sketch447"  dims[d2977=0.0453in d2978=0.75in d2979=0.375in d2980=0.25in d2981=0.5635in d2982=1.0in d2983=0.0in]
  sketch  "Sketch448"  dims[d2984=0.032in d2985=0.75in d2986=0.375in d2987=0.25in d2988=0.5635in d2989=1.0in d2990=0.0in]
  sketch  "Sketch449"  dims[d2991=0.032in d2992=0.75in d2993=0.375in d2994=0.25in d2995=0.5635in d2996=1.0in d2997=0.0in d2998=0.13in d2999=0.0in]
  sketch  "Sketch450"  dims[d3000=0.13in d3001=0.0in d3002=0.13in d3003=0.0in]
  sketch  "Sketch451"  dims[d3004=0.13in d3005=0.0in]
  sketch  "Sketch452"  dims[d3006=0.2953in d3007=0.75in d3008=0.375in d3009=0.25in d3010=0.5635in d3011=1.0in d3012=0.0in]
  sketch  "Sketch453"  dims[d3020=0.2953in d3021=0.75in d3022=0.375in d3023=0.25in d3024=0.5635in d3025=1.0in d3026=0.0in d3027=0.13in d3028=0.0in]
  sketch  "Sketch455"  dims[d3047=0.2953in d3048=0.75in d3049=0.375in d3050=0.25in d3051=0.5635in d3052=1.0in d3053=0.0in]
  sketch  "Sketch456"  dims[d3054=0.2953in d3055=0.75in d3056=0.375in d3057=0.25in d3058=0.5635in d3059=1.0in d3060=0.0in]
  sketch  "Sketch461"  dims[d3061=0.2953in d3062=0.75in d3063=0.375in d3064=0.25in d3065=0.5635in d3066=1.0in d3067=0.0in]
  sketch  "Sketch462"  dims[d3068=0.2953in d3069=0.75in d3070=0.375in d3071=0.25in d3072=0.5635in d3073=1.0in d3074=0.0in d3075=0.0614in]
  sketch  "Sketch463"  dims[d3077=-0.0614in]
  sketch  "Sketch464"  dims[d3079=0.032in d3080=0.75in d3081=0.375in d3082=0.25in d3083=0.5635in d3084=1.0in d3085=0.0in]
  other  "img_Top"
  other  "G_-1346657281_TopDecalImage"
  other  "img_Bottom"
  other  "G_-1346657281_BottomDecalImage"
  sketch  "Sketch467"  dims[d3086=0.032in d3087=0.75in d3088=0.375in d3089=0.25in d3090=0.5635in d3091=1.0in d3092=0.0in]
  sketch  "Sketch468"  dims[d3093=0.032in d3094=0.75in d3095=0.375in d3096=0.25in d3097=0.5635in d3098=1.0in d3099=0.0in]
  sketch  "Sketch469"  dims[d3100=0.032in d3101=0.75in d3102=0.375in d3103=0.25in d3104=0.5635in d3105=1.0in d3106=0.0in]
  sketch  "Sketch470"  dims[d3107=0.032in d3108=0.75in d3109=0.375in d3110=0.25in d3111=0.5635in d3112=1.0in d3113=0.0in]
  sketch  "Sketch471"  dims[d3114=0.032in d3115=0.75in d3116=0.375in d3117=0.25in d3118=0.5635in d3119=1.0in d3120=0.0in]
  sketch  "Sketch472"  dims[d3121=0.032in d3122=0.75in d3123=0.375in d3124=0.25in d3125=0.5635in d3126=1.0in d3127=0.0in]
  sketch  "Sketch473"  dims[d3128=0.032in d3129=0.75in d3130=0.375in d3131=0.25in d3132=0.5635in d3133=1.0in d3134=0.0in]
  sketch  "Sketch474"  dims[d3135=0.032in d3136=0.75in d3137=0.375in d3138=0.25in d3139=0.5635in d3140=1.0in d3141=0.0in]
  sketch  "Sketch475"  dims[d3142=0.032in d3143=0.75in d3144=0.375in d3145=0.25in d3146=0.5635in d3147=1.0in d3148=0.0in]
  sketch  "Sketch476"  dims[d3149=0.032in d3150=0.75in d3151=0.375in d3152=0.25in d3153=0.5635in d3154=1.0in d3155=0.0in]
  sketch  "Sketch477"  dims[d3156=0.032in d3157=0.75in d3158=0.375in d3159=0.25in d3160=0.5635in d3161=1.0in d3162=0.0in]
  sketch  "Sketch478"  dims[d3163=0.032in d3164=0.75in d3165=0.375in d3166=0.25in d3167=0.5635in d3168=1.0in d3169=0.0in]
  sketch  "Sketch479"  dims[d3170=0.032in d3171=0.75in d3172=0.375in d3173=0.25in d3174=0.5635in d3175=1.0in d3176=0.0in]
  sketch  "Sketch480"  dims[d3177=0.032in d3178=0.75in d3179=0.375in d3180=0.25in d3181=0.5635in d3182=1.0in d3183=0.0in]
  sketch  "Sketch481"  dims[d3184=0.032in d3185=0.75in d3186=0.375in d3187=0.25in d3188=0.5635in d3189=1.0in d3190=0.0in]
  sketch  "Sketch482"  dims[d3191=0.0315in d3192=0.75in d3193=0.375in d3194=0.25in d3195=0.5635in d3196=1.0in d3197=0.0in]
  sketch  "Sketch483"  dims[d3198=0.0315in d3199=0.75in d3200=0.375in d3201=0.25in d3202=0.5635in d3203=1.0in d3204=0.0in]
  sketch  "Sketch484"  dims[d3205=0.0315in d3206=0.75in d3207=0.375in d3208=0.25in d3209=0.5635in d3210=1.0in d3211=0.0in]
  sketch  "Sketch485"  dims[d3212=0.0315in d3213=0.75in d3214=0.375in d3215=0.25in d3216=0.5635in d3217=1.0in d3218=0.0in]
  sketch  "Sketch486"  dims[d3219=0.0315in d3220=0.75in d3221=0.375in d3222=0.25in d3223=0.5635in d3224=1.0in d3225=0.0in]
  sketch  "Sketch487"  dims[d3226=0.0315in d3227=0.75in d3228=0.375in d3229=0.25in d3230=0.5635in d3231=1.0in d3232=0.0in]
  sketch  "Sketch488"  dims[d3233=0.0315in d3234=0.75in d3235=0.375in d3236=0.25in d3237=0.5635in d3238=1.0in d3239=0.0in]
  sketch  "Sketch489"  dims[d3240=0.0315in d3241=0.75in d3242=0.375in d3243=0.25in d3244=0.5635in d3245=1.0in d3246=0.0in]
  sketch  "Sketch490"  dims[d3247=0.0315in d3248=0.75in d3249=0.375in d3250=0.25in d3251=0.5635in d3252=1.0in d3253=0.0in]
  sketch  "Sketch491"  dims[d3254=0.0315in d3255=0.75in d3256=0.375in d3257=0.25in d3258=0.5635in d3259=1.0in d3260=0.0in]
  sketch  "Sketch492"  dims[d3261=0.0315in d3262=0.75in d3263=0.375in d3264=0.25in d3265=0.5635in d3266=1.0in d3267=0.0in]
  sketch  "Sketch493"  dims[d3268=0.0315in d3269=0.75in d3270=0.375in d3271=0.25in d3272=0.5635in d3273=1.0in d3274=0.0in]
  sketch  "Sketch494"  dims[d3275=0.0453in d3276=0.75in d3277=0.375in d3278=0.25in d3279=0.5635in d3280=1.0in d3281=0.0in]
  sketch  "Sketch495"  dims[d3282=0.0453in d3283=0.75in d3284=0.375in d3285=0.25in d3286=0.5635in d3287=1.0in d3288=0.0in]
  sketch  "Sketch496"  dims[d3289=0.0453in d3290=0.75in d3291=0.375in d3292=0.25in d3293=0.5635in d3294=1.0in d3295=0.0in]
  sketch  "Sketch497"  dims[d3296=0.0453in d3297=0.75in d3298=0.375in d3299=0.25in d3300=0.5635in d3301=1.0in d3302=0.0in]
  sketch  "Sketch498"  dims[d3303=0.0453in d3304=0.75in d3305=0.375in d3306=0.25in d3307=0.5635in d3308=1.0in d3309=0.0in]
  sketch  "Sketch499"  dims[d3310=0.0453in d3311=0.75in d3312=0.375in d3313=0.25in d3314=0.5635in d3315=1.0in d3316=0.0in]
  sketch  "Sketch500"  dims[d3317=0.0453in d3318=0.75in d3319=0.375in d3320=0.25in d3321=0.5635in d3322=1.0in d3323=0.0in]
  sketch  "Sketch501"  dims[d3324=0.0453in d3325=0.75in d3326=0.375in d3327=0.25in d3328=0.5635in d3329=1.0in d3330=0.0in]
  sketch  "Sketch502"  dims[d3331=0.032in d3332=0.75in d3333=0.375in d3334=0.25in d3335=0.5635in d3336=1.0in d3337=0.0in]
  sketch  "Sketch503"  dims[d3338=0.032in d3339=0.75in d3340=0.375in d3341=0.25in d3342=0.5635in d3343=1.0in d3344=0.0in]
  sketch  "Sketch504"  dims[d3345=0.032in d3346=0.75in d3347=0.375in d3348=0.25in d3349=0.5635in d3350=1.0in d3351=0.0in]
  sketch  "Sketch505"  dims[d3352=0.032in d3353=0.75in d3354=0.375in d3355=0.25in d3356=0.5635in d3357=1.0in d3358=0.0in]
  sketch  "Sketch506"  dims[d3359=0.032in d3360=0.75in d3361=0.375in d3362=0.25in d3363=0.5635in d3364=1.0in d3365=0.0in]
  sketch  "Sketch507"  dims[d3366=0.032in d3367=0.75in d3368=0.375in d3369=0.25in d3370=0.5635in d3371=1.0in d3372=0.0in]
  sketch  "Sketch508"  dims[d3373=0.032in d3374=0.75in d3375=0.375in d3376=0.25in d3377=0.5635in d3378=1.0in d3379=0.0in]
  sketch  "Sketch509"  dims[d3380=0.032in d3381=0.75in d3382=0.375in d3383=0.25in d3384=0.5635in d3385=1.0in d3386=0.0in]
  sketch  "Sketch510"  dims[d3387=0.032in d3388=0.75in d3389=0.375in d3390=0.25in d3391=0.5635in d3392=1.0in d3393=0.0in]
  sketch  "Sketch511"  dims[d3394=0.032in d3395=0.75in d3396=0.375in d3397=0.25in d3398=0.5635in d3399=1.0in d3400=0.0in]
  sketch  "Sketch512"  dims[d3401=0.032in d3402=0.75in d3403=0.375in d3404=0.25in d3405=0.5635in d3406=1.0in d3407=0.0in]
  sketch  "Sketch513"  dims[d3408=0.032in d3409=0.75in d3410=0.375in d3411=0.25in d3412=0.5635in d3413=1.0in d3414=0.0in]
  sketch  "Sketch514"  dims[d3415=0.032in d3416=0.75in d3417=0.375in d3418=0.25in d3419=0.5635in d3420=1.0in d3421=0.0in]
  sketch  "Sketch515"  dims[d3422=0.032in d3423=0.75in d3424=0.375in d3425=0.25in d3426=0.5635in d3427=1.0in d3428=0.0in]
  sketch  "Sketch516"  dims[d3429=0.032in d3430=0.75in d3431=0.375in d3432=0.25in d3433=0.5635in d3434=1.0in d3435=0.0in]
  sketch  "Sketch517"  dims[d3436=0.032in d3437=0.75in d3438=0.375in d3439=0.25in d3440=0.5635in d3441=1.0in d3442=0.0in]
  sketch  "Sketch518"
note: 301 required parameter values undecoded (feature->parameter linkage not recoverable at this tier; creation-order binding heuristic only, values carry confidence <= 0.55)
